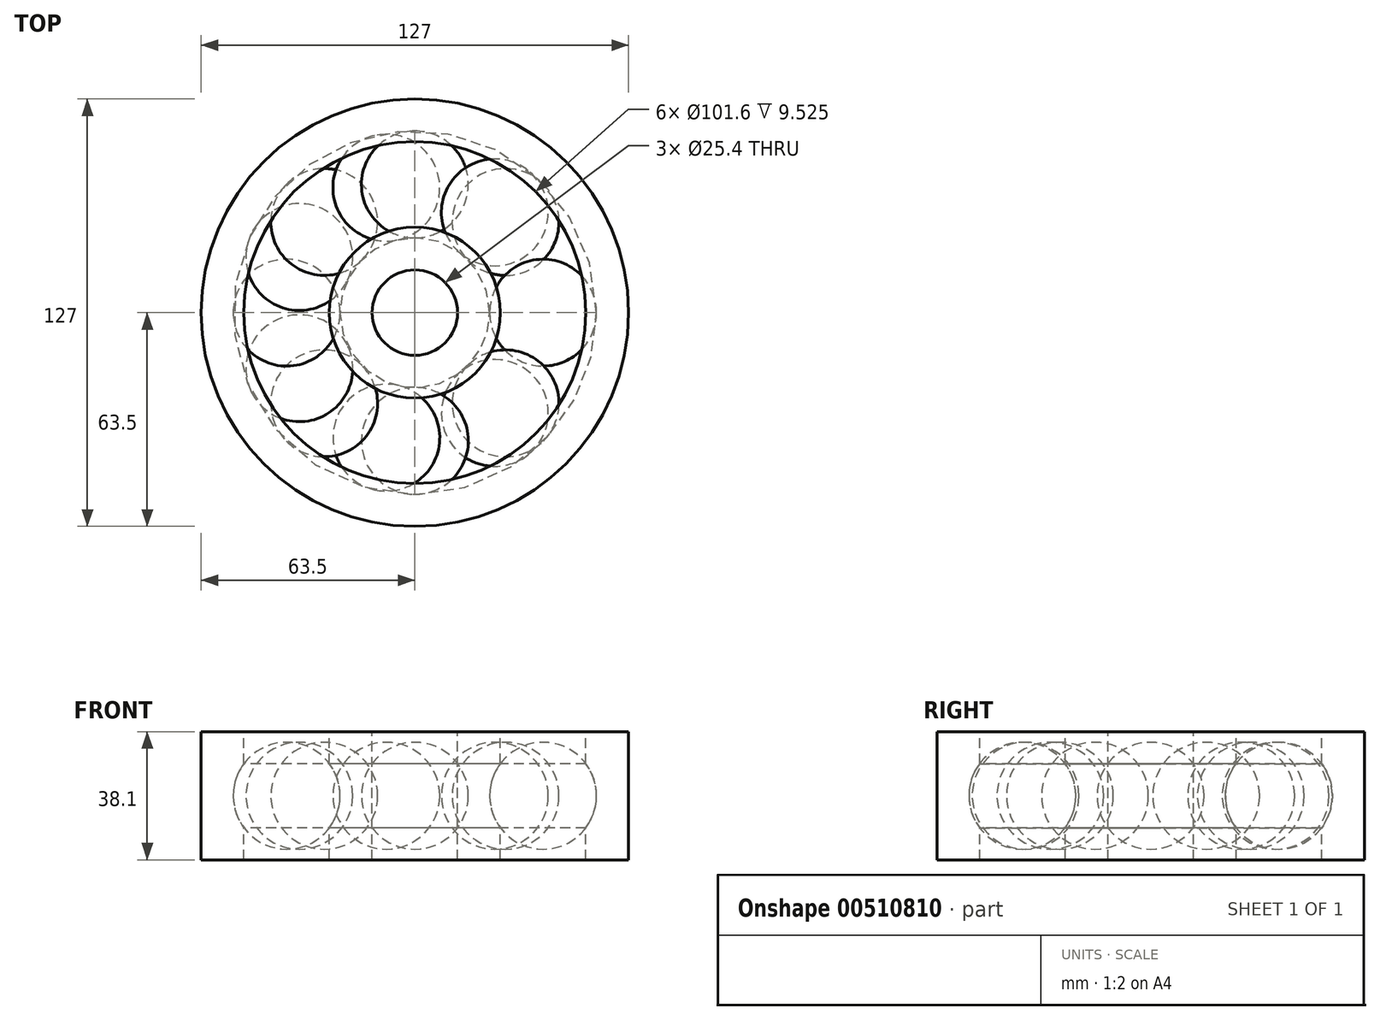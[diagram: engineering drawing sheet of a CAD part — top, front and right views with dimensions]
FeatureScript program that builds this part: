
annotation { "Feature Type Name" : "Feature", "Feature Type Description" : "" }
export const myFeature = defineFeature(function(context is Context, id is Id, definition is map)
    precondition{}
    {
        {
            var Q0;
            Q0=qCreatedBy(makeId("Front.planeOp"),FACE);
            var sketch = newSketch(context, id + "F0", { "sketchPlane" : qUnion([Q0])});
            skLineSegment(sketch, "E0", {"start": v(0, 19.05) * mm, "end": v(0, -19.05) * mm, "construction": true});
            skLineSegment(sketch, "E1", {"start": v(12.7, 19.05) * mm, "end": v(12.7, -19.05) * mm});
            skLineSegment(sketch, "E2", {"start": v(12.7, -19.05) * mm, "end": v(25.4, -19.05) * mm});
            skLineSegment(sketch, "E3", {"start": v(25.4, -19.05) * mm, "end": v(25.4, 19.05) * mm});
            skLineSegment(sketch, "E4", {"start": v(25.4, 19.05) * mm, "end": v(12.7, 19.05) * mm});
            skCircle(sketch, "E5", {"center": v(38.1, 0) * mm, "radius": 15.88 * mm});
            skLineSegment(sketch, "E6.bottom", {"start": v(50.8, 19.05) * mm, "end": v(63.5, 19.05) * mm});
            skLineSegment(sketch, "E6.top", {"start": v(50.8, -19.05) * mm, "end": v(63.5, -19.05) * mm});
            skLineSegment(sketch, "E6.left", {"start": v(50.8, 19.05) * mm, "end": v(50.8, -19.05) * mm});
            skLineSegment(sketch, "E6.right", {"start": v(63.5, 19.05) * mm, "end": v(63.5, -19.05) * mm});
            skLineSegment(sketch, "E7", {"start": v(22.22, 0) * mm, "end": v(53.97, 0) * mm});
            skLineSegment(sketch, "E8", {"start": v(12.7, 0) * mm, "end": v(22.22, 0) * mm, "construction": true});
            skLineSegment(sketch, "E9", {"start": v(53.97, 0) * mm, "end": v(63.5, 0) * mm, "construction": true});
            skSolve(sketch);
        }
        {
            var Q0;
            Q0=makeQuery(id+"F0.imprint","IMPRINT",FACE,{"disambiguationData":[TD([[makeQuery(id+"F0.imprint","IMPRINT",EDGE,{"derivedFrom":sQuery(id+"F0.wireOp",EDGE,"E1")}),1.0]])]});
            var Q1;
            {var subQ1=sQuery(id+"F0.wireOp",EDGE,"E6.bottom");Q1=makeQuery(id+"F0.imprint","IMPRINT",FACE,{"disambiguationData":[TD([[makeQuery(id+"F0.imprint","IMPRINT",EDGE,{"derivedFrom":subQ1}),-1.0]])]});}
            var Q2;
            Q2=sQuery(id+"F0.wireOp",EDGE,"E0");
            revolve(context, id + "F1", {"entities" : qUnion([Q0, Q1]), "axis" : qUnion([Q2]), "revolveType" : RevolveType.FULL});
        }
        {
            var Q0;
            {var subQ0=sQuery(id+"F0.wireOp",EDGE,"E5");var subQ1=sQuery(id+"F0.wireOp",EDGE,"E3");var subQ2=makeQuery(id+"F0.imprint","INTERSECT",VERTEX,{"disambiguationData":[OD(1.0)],"derivedFrom":[subQ1,subQ0]});Q0=makeQuery(id+"F0.imprint","IMPRINT",FACE,{"disambiguationData":[TD([[makeQuery(id+"F0.imprint","IMPRINT",EDGE,{"disambiguationData":[TD([[subQ2,1.0]])],"derivedFrom":subQ1}),-1.0]])]});}
            var Q1;
            {var subQ0=sQuery(id+"F0.wireOp",EDGE,"E5");var subQ1=sQuery(id+"F0.wireOp",EDGE,"E3");var subQ2=makeQuery(id+"F0.imprint","INTERSECT",VERTEX,{"disambiguationData":[OD(1.0)],"derivedFrom":[subQ1,subQ0]});Q1=makeQuery(id+"F0.imprint","IMPRINT",FACE,{"disambiguationData":[TD([[makeQuery(id+"F0.imprint","IMPRINT",EDGE,{"disambiguationData":[TD([[subQ2,1.0]])],"derivedFrom":subQ1}),1.0]])]});}
            var Q2;
            {var subQ0=sQuery(id+"F0.wireOp",EDGE,"E7");var subQ1=sQuery(id+"F0.wireOp",EDGE,"E5");var subQ2=makeQuery(id+"F0.imprint","INTERSECT",VERTEX,{"disambiguationData":[OD(1.0)],"derivedFrom":[subQ1,subQ0]});Q2=makeQuery(id+"F0.imprint","IMPRINT",FACE,{"disambiguationData":[TD([[makeQuery(id+"F0.imprint","IMPRINT",EDGE,{"disambiguationData":[TD([[subQ2,-1.0]])],"derivedFrom":subQ1}),1.0]])]});}
            var Q3;
            Q3=sQuery(id+"F0.wireOp",EDGE,"E7");
            revolve(context, id + "F2", {"entities" : qUnion([Q0, Q1, Q2]), "axis" : qUnion([Q3]), "revolveType" : RevolveType.FULL});
        }
        {
            var Q0;
            Q0=makeQuery(id+"F2.opRevolve","SWEPT_BODY",BODY,{"disambiguationData":[OSD([sQuery(id+"F0.wireOp",EDGE,"E5"),sQuery(id+"F0.wireOp",EDGE,"E7")])]});
            var Q1;
            Q1=sQuery(id+"F0.wireOp",EDGE,"E0");
            circularPattern(context, id + "F3", {"entities" : qUnion([Q0]), "axis" : qUnion([Q1]), "angle" : 360 * degree, "instanceCount" : 7, "equalSpace" : true});
        }
        {
            var Q0;
            Q0=makeQuery(id+"F0.imprint","IMPRINT",FACE,{"disambiguationData":[TD([[makeQuery(id+"F0.imprint","IMPRINT",EDGE,{"derivedFrom":sQuery(id+"F0.wireOp",EDGE,"E1")}),1.0]])]});
            var Q1;
            {var subQ1=sQuery(id+"F0.wireOp",EDGE,"E6.bottom");Q1=makeQuery(id+"F0.imprint","IMPRINT",FACE,{"disambiguationData":[TD([[makeQuery(id+"F0.imprint","IMPRINT",EDGE,{"derivedFrom":subQ1}),-1.0]])]});}
            var Q2;
            Q2=sQuery(id+"F0.wireOp",EDGE,"E0");
            revolve(context, id + "F4", {"entities" : qUnion([Q0, Q1]), "axis" : qUnion([Q2]), "revolveType" : RevolveType.FULL});
        }
        {
            var Q0;
            {var subQ0=sQuery(id+"F0.wireOp",EDGE,"E5");var subQ1=sQuery(id+"F0.wireOp",EDGE,"E3");var subQ2=makeQuery(id+"F0.imprint","INTERSECT",VERTEX,{"disambiguationData":[OD(1.0)],"derivedFrom":[subQ1,subQ0]});Q0=makeQuery(id+"F0.imprint","IMPRINT",FACE,{"disambiguationData":[TD([[makeQuery(id+"F0.imprint","IMPRINT",EDGE,{"disambiguationData":[TD([[subQ2,1.0]])],"derivedFrom":subQ1}),1.0]])]});}
            var Q1;
            {var subQ0=sQuery(id+"F0.wireOp",EDGE,"E5");var subQ1=sQuery(id+"F0.wireOp",EDGE,"E3");var subQ2=makeQuery(id+"F0.imprint","INTERSECT",VERTEX,{"disambiguationData":[OD(1.0)],"derivedFrom":[subQ1,subQ0]});Q1=makeQuery(id+"F0.imprint","IMPRINT",FACE,{"disambiguationData":[TD([[makeQuery(id+"F0.imprint","IMPRINT",EDGE,{"disambiguationData":[TD([[subQ2,1.0]])],"derivedFrom":subQ1}),-1.0]])]});}
            var Q2;
            {var subQ0=sQuery(id+"F0.wireOp",EDGE,"E7");var subQ1=sQuery(id+"F0.wireOp",EDGE,"E5");var subQ2=makeQuery(id+"F0.imprint","INTERSECT",VERTEX,{"disambiguationData":[OD(1.0)],"derivedFrom":[subQ1,subQ0]});Q2=makeQuery(id+"F0.imprint","IMPRINT",FACE,{"disambiguationData":[TD([[makeQuery(id+"F0.imprint","IMPRINT",EDGE,{"disambiguationData":[TD([[subQ2,-1.0]])],"derivedFrom":subQ1}),1.0]])]});}
            var Q3;
            Q3=sQuery(id+"F0.wireOp",EDGE,"E7");
            revolve(context, id + "F5", {"entities" : qUnion([Q0, Q1, Q2]), "axis" : qUnion([Q3]), "revolveType" : RevolveType.FULL});
        }
        {
            var Q0;
            Q0=makeQuery(id+"F5.opRevolve","SWEPT_BODY",BODY,{"disambiguationData":[OSD([sQuery(id+"F0.wireOp",EDGE,"E5"),sQuery(id+"F0.wireOp",EDGE,"E7")])]});
            var Q1;
            Q1=sQuery(id+"F0.wireOp",EDGE,"E0");
            circularPattern(context, id + "F6", {"entities" : qUnion([Q0]), "axis" : qUnion([Q1]), "angle" : 360 * degree, "instanceCount" : 8, "equalSpace" : true});
        }
        {
            var Q0;
            Q0=makeQuery(id+"F0.imprint","IMPRINT",FACE,{"disambiguationData":[TD([[makeQuery(id+"F0.imprint","IMPRINT",EDGE,{"derivedFrom":sQuery(id+"F0.wireOp",EDGE,"E1")}),1.0]])]});
            var Q1;
            {var subQ6=sQuery(id+"F0.wireOp",EDGE,"E6.bottom");Q1=makeQuery(id+"F0.imprint","IMPRINT",FACE,{"disambiguationData":[TD([[makeQuery(id+"F0.imprint","IMPRINT",EDGE,{"derivedFrom":subQ6}),-1.0]])]});}
            var Q2;
            Q2=sQuery(id+"F0.wireOp",EDGE,"E0");
            revolve(context, id + "F7", {"entities" : qUnion([Q0, Q1]), "axis" : qUnion([Q2]), "revolveType" : RevolveType.FULL});
        }
        {
            var Q0;
            Q0=makeQuery(id+"F5.opRevolve","SWEPT_BODY",BODY,{"disambiguationData":[OSD([sQuery(id+"F0.wireOp",EDGE,"E5"),sQuery(id+"F0.wireOp",EDGE,"E7")])]});
            var Q1;
            Q1=sQuery(id+"F0.wireOp",EDGE,"E0");
            circularPattern(context, id + "F8", {"entities" : qUnion([Q0]), "axis" : qUnion([Q1]), "angle" : 360 * degree, "instanceCount" : 7, "equalSpace" : true});
        }
    });
